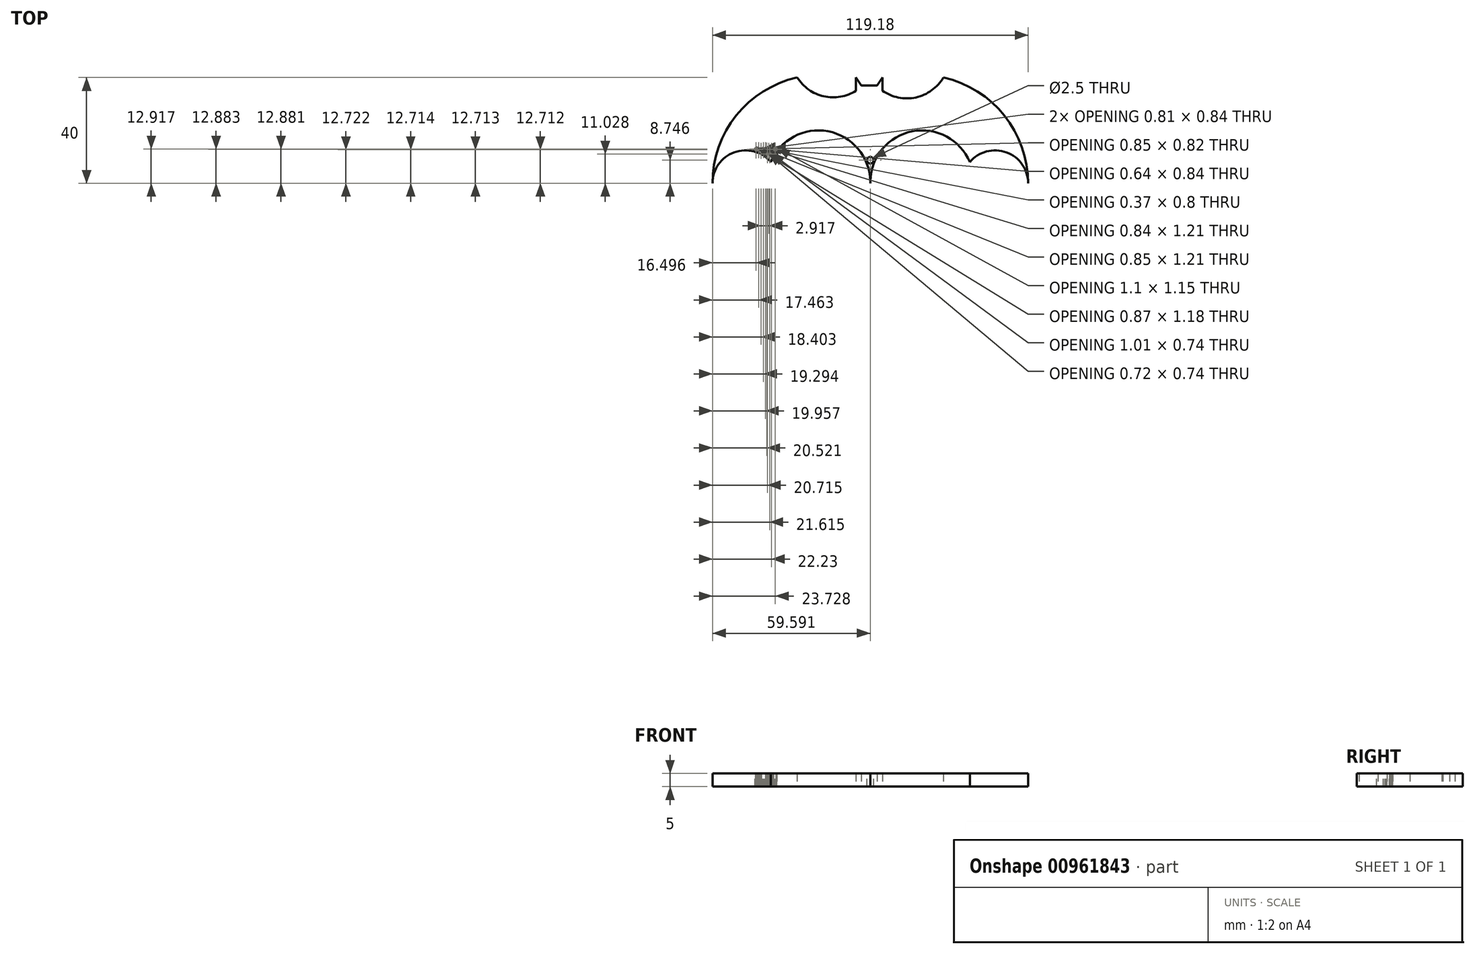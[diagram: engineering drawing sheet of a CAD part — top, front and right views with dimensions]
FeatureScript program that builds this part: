
annotation { "Feature Type Name" : "Feature", "Feature Type Description" : "" }
export const myFeature = defineFeature(function(context is Context, id is Id, definition is map)
    precondition{}
    {
        {
            var Q0;
            Q0=qCreatedBy(makeId("Top.planeOp"),FACE);
            var sketch = newSketch(context, id + "F0", { "sketchPlane" : qUnion([Q0])});
            skArc(sketch, "E0", {"start": v(58.2, -8) * mm, "mid": v(50, 3.7) * mm, "end": v(36.2, 0) * mm});
            skArc(sketch, "E1", {"start": v(-39, 0) * mm, "mid": v(-52.8, 3.7) * mm, "end": v(-61, -8) * mm});
            skArc(sketch, "E2", {"start": v(-1.4, -8) * mm, "mid": v(-16.88, 11.57) * mm, "end": v(-39, 0) * mm});
            skArc(sketch, "E3", {"start": v(36.2, 0) * mm, "mid": v(14.08, 11.57) * mm, "end": v(-1.4, -8) * mm});
            skLineSegment(sketch, "E4", {"start": v(-4.8, 29) * mm, "end": v(-6.8, 32) * mm});
            skLineSegment(sketch, "E5", {"start": v(1.2, 29) * mm, "end": v(3.2, 32) * mm});
            skLineSegment(sketch, "E6", {"start": v(-4.8, 29) * mm, "end": v(1.2, 29) * mm});
            skPoint(sketch, "E7", {"position": v(-29, 32) * mm});
            skArc(sketch, "E8", {"start": v(-29, 32) * mm, "mid": v(-52, 17.61) * mm, "end": v(-61, -8) * mm});
            skArc(sketch, "E9", {"start": v(58.2, -8) * mm, "mid": v(49.2, 17.61) * mm, "end": v(26.2, 32) * mm});
            skLineSegment(sketch, "E10", {"start": v(-6.8, 32) * mm, "end": v(-6.8, 27) * mm});
            skLineSegment(sketch, "E11", {"start": v(3.2, 32) * mm, "end": v(3.2, 27) * mm});
            skArc(sketch, "E12", {"start": v(-29, 32) * mm, "mid": v(-18.94, 24.87) * mm, "end": v(-6.8, 27) * mm});
            skArc(sketch, "E13", {"start": v(3.2, 27) * mm, "mid": v(15.8, 24.46) * mm, "end": v(26.2, 32) * mm});
            skSolve(sketch);
        }
        {
            var Q0;
            Q0 = qSketchRegion(id + "F0", true);
            extrude(context, id + "F1", {"entities" : qUnion([Q0]), "depth" : 5 * mm, "offsetDistance" : 25 * mm});
        }
        {
            var Q0;
            Q0=makeQuery(id+"F1.opExtrude","CAP_FACE",FACE,{"disambiguationData":[OSD([sQuery(id+"F0.wireOp",EDGE,"E0"),sQuery(id+"F0.wireOp",EDGE,"E1"),sQuery(id+"F0.wireOp",EDGE,"E2"),sQuery(id+"F0.wireOp",EDGE,"E3"),sQuery(id+"F0.wireOp",EDGE,"E4"),sQuery(id+"F0.wireOp",EDGE,"E5"),sQuery(id+"F0.wireOp",EDGE,"E6"),sQuery(id+"F0.wireOp",EDGE,"E8"),sQuery(id+"F0.wireOp",EDGE,"E9"),sQuery(id+"F0.wireOp",EDGE,"E10"),sQuery(id+"F0.wireOp",EDGE,"E11"),sQuery(id+"F0.wireOp",EDGE,"E12"),sQuery(id+"F0.wireOp",EDGE,"E13")])],"isStart":false});
            var sketch = newSketch(context, id + "F2", { "sketchPlane" : qUnion([Q0])});
            skText(sketch, "E14", { "text": "Shakisan.R", "fontName": "Tinos-BoldItalic.ttf"});
            const initialGuessF2  = {"E14": [-0.04496, 0.00431, 1, 0, 0.00126]};
            skSetInitialGuess(sketch, initialGuessF2);
            skSolve(sketch);
        }
        {
            var Q0;
            Q0 = qSketchRegion(id + "F2", true);
            extrude(context, id + "F3", {"entities" : qUnion([Q0]), "operationType" : NewBodyOperationType.REMOVE, "oppositeDirection" : true, "depth" : 25 * mm, "offsetDistance" : 25 * mm});
        }
        {
            var Q0;
            {var subQ0=sQuery(id+"F0.wireOp",EDGE,"E10");var subQ1=sQuery(id+"F0.wireOp",EDGE,"E8");var subQ2=sQuery(id+"F0.wireOp",EDGE,"E6");var subQ3=sQuery(id+"F0.wireOp",EDGE,"E4");var subQ4=sQuery(id+"F0.wireOp",EDGE,"E5");var subQ5=sQuery(id+"F0.wireOp",EDGE,"E0");var subQ6=sQuery(id+"F0.wireOp",EDGE,"E9");var subQ7=sQuery(id+"F0.wireOp",EDGE,"E1");var subQ8=sQuery(id+"F0.wireOp",EDGE,"E3");var subQ9=sQuery(id+"F0.wireOp",EDGE,"E2");var subQ11=sQuery(id+"F0.wireOp",EDGE,"E11");var subQ12=sQuery(id+"F0.wireOp",EDGE,"E12");var subQ13=sQuery(id+"F0.wireOp",EDGE,"E13");Q0=makeQuery(id+"F3.boolean.opBoolean","SPLIT",FACE,{"disambiguationData":[TD([makeQuery(id+"F1.opExtrude","SWEPT_FACE",FACE,{"disambiguationData":[OSD([subQ5])]})])],"derivedFrom":makeQuery(id+"F1.opExtrude","CAP_FACE",FACE,{"disambiguationData":[OSD([subQ5,subQ7,subQ9,subQ8,subQ3,subQ4,subQ2,subQ1,subQ6,subQ0,subQ11,subQ12,subQ13])],"isStart":false})});}
            var sketch = newSketch(context, id + "F4", { "sketchPlane" : qUnion([Q0])});
            skText(sketch, "E15", { "text": "TM", "fontName": "Tinos-Bold.ttf"});
            const initialGuessF4  = {"E15": [-0.04065, 0.00266, 1, 0, 0.00081]};
            skSetInitialGuess(sketch, initialGuessF4);
            skSolve(sketch);
        }
        {
            var Q0;
            Q0 = qSketchRegion(id + "F4", true);
            extrude(context, id + "F5", {"entities" : qUnion([Q0]), "operationType" : NewBodyOperationType.REMOVE, "oppositeDirection" : true, "depth" : 25 * mm, "offsetDistance" : 25 * mm});
        }
        {
            var Q0;
            {var subQ0=sQuery(id+"F0.wireOp",EDGE,"E10");var subQ1=sQuery(id+"F0.wireOp",EDGE,"E8");var subQ2=sQuery(id+"F0.wireOp",EDGE,"E6");var subQ3=sQuery(id+"F0.wireOp",EDGE,"E4");var subQ4=sQuery(id+"F0.wireOp",EDGE,"E5");var subQ5=sQuery(id+"F0.wireOp",EDGE,"E0");var subQ6=sQuery(id+"F0.wireOp",EDGE,"E9");var subQ7=sQuery(id+"F0.wireOp",EDGE,"E1");var subQ8=sQuery(id+"F0.wireOp",EDGE,"E3");var subQ9=sQuery(id+"F0.wireOp",EDGE,"E2");var subQ11=sQuery(id+"F0.wireOp",EDGE,"E11");var subQ12=sQuery(id+"F0.wireOp",EDGE,"E12");var subQ13=sQuery(id+"F0.wireOp",EDGE,"E13");Q0=makeQuery(id+"F3.boolean.opBoolean","SPLIT",FACE,{"disambiguationData":[TD([makeQuery(id+"F1.opExtrude","SWEPT_FACE",FACE,{"disambiguationData":[OSD([subQ5])]})])],"derivedFrom":makeQuery(id+"F1.opExtrude","CAP_FACE",FACE,{"disambiguationData":[OSD([subQ5,subQ7,subQ9,subQ8,subQ3,subQ4,subQ2,subQ1,subQ6,subQ0,subQ11,subQ12,subQ13])],"isStart":false})});}
            var sketch = newSketch(context, id + "F6", { "sketchPlane" : qUnion([Q0])});
            skCircle(sketch, "E16", {"center": v(-1.4, 0.75) * mm, "radius": 1.25 * mm});
            skPoint(sketch, "E17.start.orphan", {"position": v(-3.24, 0.75) * mm});
            skPoint(sketch, "E18.trimOffspring.end.orphan", {"position": v(0.45, 0.75) * mm});
            skSolve(sketch);
        }
        {
            var Q0;
            Q0=makeQuery(id+"F6.imprint","IMPRINT",FACE,{"disambiguationData":[TD([[makeQuery(id+"F6.imprint","IMPRINT",EDGE,{"derivedFrom":sQuery(id+"F6.wireOp",EDGE,"E16")}),1.0]])]});
            extrude(context, id + "F7", {"entities" : qUnion([Q0]), "operationType" : NewBodyOperationType.REMOVE, "oppositeDirection" : true, "depth" : 25 * mm, "offsetDistance" : 25 * mm});
        }
    });
